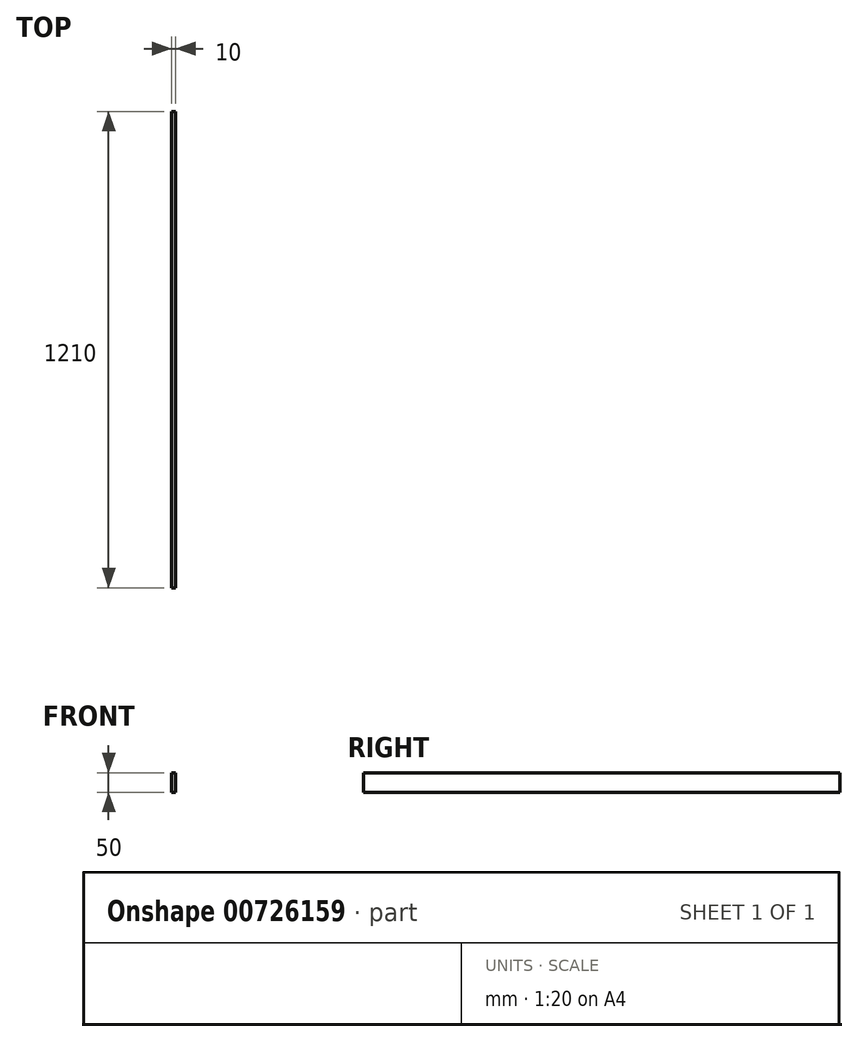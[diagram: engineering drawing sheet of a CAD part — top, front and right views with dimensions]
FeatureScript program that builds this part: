
annotation { "Feature Type Name" : "Feature", "Feature Type Description" : "" }
export const myFeature = defineFeature(function(context is Context, id is Id, definition is map)
    precondition{}
    {
        {
            var Q0;
            Q0=qCreatedBy(makeId("Right.planeOp"),FACE);
            var sketch = newSketch(context, id + "F0", { "sketchPlane" : qUnion([Q0])});
            skLineSegment(sketch, "E0.bottom", {"start": v(-605, 25) * mm, "end": v(605, 25) * mm});
            skLineSegment(sketch, "E0.top", {"start": v(-605, -25) * mm, "end": v(605, -25) * mm});
            skLineSegment(sketch, "E0.left", {"start": v(-605, 25) * mm, "end": v(-605, -25) * mm});
            skLineSegment(sketch, "E0.right", {"start": v(605, 25) * mm, "end": v(605, -25) * mm});
            skLineSegment(sketch, "E1", {"start": v(0, -25) * mm, "end": v(0, 25) * mm, "construction": true});
            skSolve(sketch);
        }
        {
            var Q0;
            Q0 = qSketchRegion(id + "F0", true);
            extrude(context, id + "F1", {"entities" : qUnion([Q0]), "depth" : 10 * mm, "offsetDistance" : 25 * mm});
        }
    });
